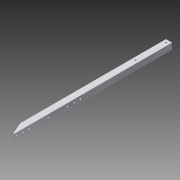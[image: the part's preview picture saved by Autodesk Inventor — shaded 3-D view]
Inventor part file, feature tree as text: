
AUTODESK INVENTOR PART (.ipt)
format: ipt  version: 2015 (Build 190159000, 159)  size: 147,968 bytes
history: native  units: in
note: dims shown in document units (in); Inventor stores cm internally (conversion verified against a paired STEP export)
features: sketch x5, hole x3, extrude x2, projected_geometry x1
ambient origin geometry x8: Origin, YZ Plane, XZ Plane, XY Plane, X Axis, Y Axis, Z Axis, Center Point
bodies: Solid1 (feature_tree)
feature tree (11):
  extrude  "Extrusion1"  Depth=1.0in
  hole  "Hole1"  [1 undecoded]
  hole  "Hole2"  [1 undecoded]
  extrude  "Extrusion3"  Depth=25.875in
  hole  "Hole3"  [1 undecoded]
  sketch  "Sketch1"  dims[d0=1.0in d1=1.0in]
  sketch  "Sketch2"  dims[d2=0.75in d3=0.75in]
  sketch  "Sketch3"  dims[d4=0.125in d5=0.125in]
  sketch  "Sketch5"  dims[d6=25.875in d7=0.0in d8=0.5in]
  projected_geometry  "Projected Loop2"
  sketch  "Sketch6"  dims[d9=0.5in d10=0.5in d11=5.5in d12=0.25in d13=0.75in d14=0.375in d15=0.25in d16=0.5635in d17=1.0in d18=0.8108in d19=0.5in d20=0.5in d21=0.5in d22=1.0in d23=8.375in d24=0.5in d25=0.5in d26=1.0in d27=0.25in d28=0.75in d29=0.375in d30=0.25in d31=0.5635in d32=1.0in d33=0.8108in d37=0.875in d38=2.0in d39=1.0in d40=0.0in d41=0.5in d42=2.5in d43=5.625in d44=0.5in d45=0.5in d46=8.75in d47=0.25in d48=0.75in d49=0.375in d50=0.25in d51=0.5635in d52=1.0in d53=0.8108in]
note: 3 required parameter values undecoded (feature->parameter linkage not recoverable at this tier; creation-order binding heuristic only, values carry confidence <= 0.55)
